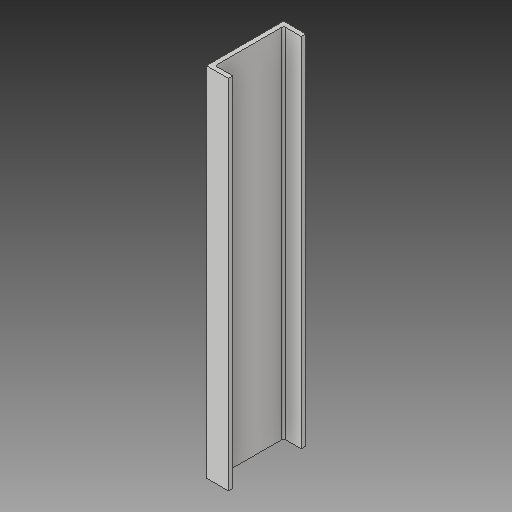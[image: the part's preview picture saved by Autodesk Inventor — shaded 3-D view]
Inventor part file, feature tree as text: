
AUTODESK INVENTOR PART (.ipt)
format: ipt  version: 2019 (Build 230136000, 136)  size: 103,424 bytes
history: native  units: in
note: dims shown in document units (in); Inventor stores cm internally (conversion verified against a paired STEP export)
features: other x3, sketch x3
ambient origin geometry x8: Origin, YZ Plane, XZ Plane, XY Plane, X Axis, Y Axis, Z Axis, Center Point
bodies: Solid1 (feature_tree)
feature tree (6):
  other  "Base1_MIR.ipt"
  other  "Solid1::Base1_MIR.ipt"
  other  "TaggingFeature1"
  sketch  "Sketch1"  dims[d0=0.3937in]
  sketch  "Sketch2"
  sketch  "Sketch3"
